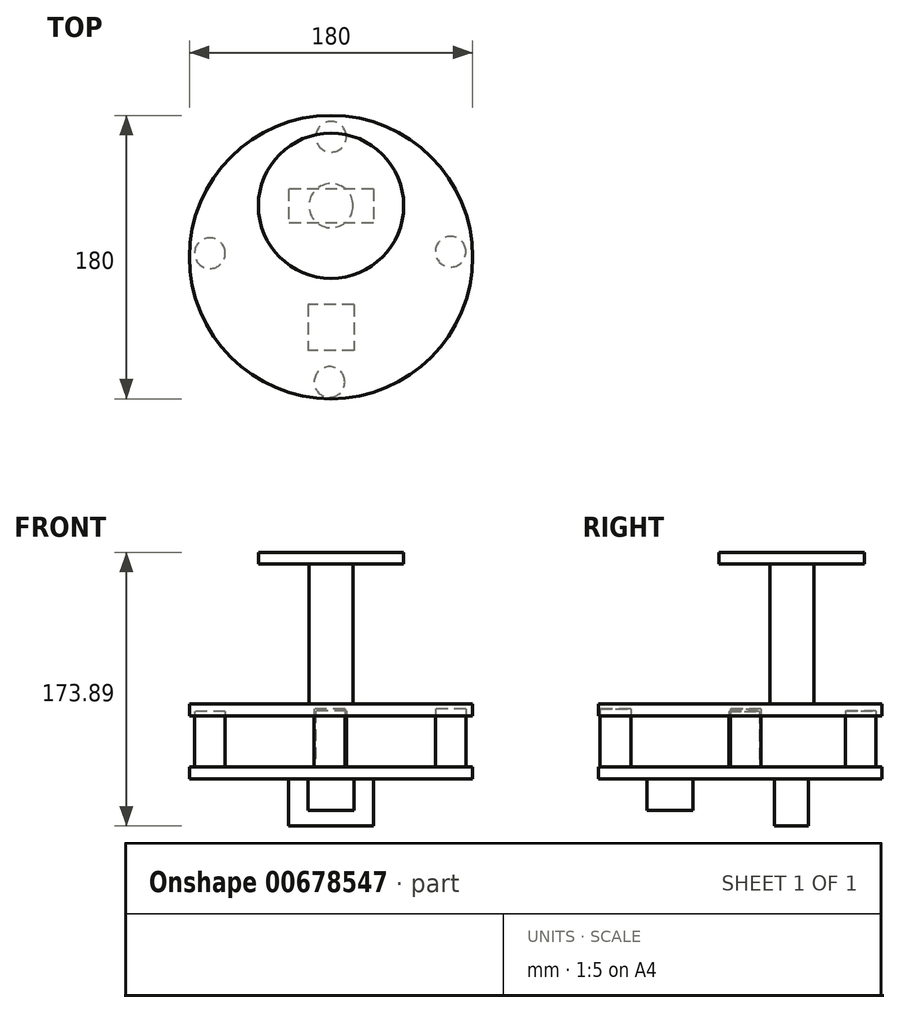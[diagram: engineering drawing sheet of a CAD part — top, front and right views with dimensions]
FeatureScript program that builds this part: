
annotation { "Feature Type Name" : "Feature", "Feature Type Description" : "" }
export const myFeature = defineFeature(function(context is Context, id is Id, definition is map)
    precondition{}
    {
        {
            var Q0;
            Q0=qCreatedBy(makeId("Top.planeOp"),FACE);
            var sketch = newSketch(context, id + "F0", { "sketchPlane" : qUnion([Q0])});
            skCircle(sketch, "E0", {"center": v(0, -4.4) * mm, "radius": 90 * mm});
            skSolve(sketch);
        }
        {
            var Q0;
            Q0 = qSketchRegion(id + "F0", true);
            extrude(context, id + "F1", {"entities" : qUnion([Q0]), "oppositeDirection" : true, "depth" : 7.5 * mm, "offsetDistance" : 25.4 * mm});
        }
        {
            var Q0;
            Q0=makeQuery(id+"F1.opExtrude","SWEPT_BODY",BODY,{"disambiguationData":[OSD([sQuery(id+"F0.wireOp",EDGE,"E0")])]});
            transform(context, id + "F2", {"entities" : qUnion([Q0]), "transformType" : TransformType.TRANSLATION_3D, "dx" : 0 * mm, "dy" : 0 * mm, "dz" : 40 * mm, "makeCopy" : true});
        }
        {
            var Q0;
            Q0=makeQuery(id+"F2.opPattern","COPY",BODY,{"derivedFrom":makeQuery(id+"F1.opExtrude","SWEPT_BODY",BODY,{"disambiguationData":[OSD([sQuery(id+"F0.wireOp",EDGE,"E0")])]}),"instanceName":"1"});
            transform(context, id + "F3", {"entities" : qUnion([Q0]), "transformType" : TransformType.TRANSLATION_3D, "dx" : 0 * mm, "dy" : 0 * mm, "dz" : 0 * mm, "makeCopy" : true});
        }
        {
            var Q0;
            Q0=makeQuery(id+"F2.opPattern","COPY",FACE,{"derivedFrom":makeQuery(id+"F1.opExtrude","CAP_FACE",FACE,{"disambiguationData":[OSD([sQuery(id+"F0.wireOp",EDGE,"E0")])],"isStart":true}),"instanceName":"1"});
            var sketch = newSketch(context, id + "F4", { "sketchPlane" : qUnion([Q0])});
            skLineSegment(sketch, "E1", {"start": v(0, 0) * mm, "end": v(0, 28.23) * mm});
            skCircle(sketch, "E2", {"center": v(0, 28.23) * mm, "radius": 14.02 * mm});
            skSolve(sketch);
        }
        {
            var Q0;
            Q0 = qSketchRegion(id + "F4", true);
            extrude(context, id + "F5", {"entities" : qUnion([Q0]), "depth" : 88.9 * mm, "offsetDistance" : 25.4 * mm});
        }
        {
            var Q0;
            Q0=makeQuery(id+"F5.opExtrude","CAP_FACE",FACE,{"disambiguationData":[OSD([sQuery(id+"F4.wireOp",EDGE,"E2")])],"isStart":false});
            var sketch = newSketch(context, id + "F6", { "sketchPlane" : qUnion([Q0])});
            skCircle(sketch, "E3", {"center": v(0, 28.23) * mm, "radius": 46.13 * mm});
            skSolve(sketch);
        }
        {
            var Q0;
            Q0 = qSketchRegion(id + "F6", true);
            extrude(context, id + "F7", {"entities" : qUnion([Q0]), "operationType" : NewBodyOperationType.ADD, "depth" : 7.5 * mm, "offsetDistance" : 25.4 * mm});
        }
        {
            var Q0;
            Q0=makeQuery(id+"F1.opExtrude","CAP_FACE",FACE,{"disambiguationData":[OSD([sQuery(id+"F0.wireOp",EDGE,"E0")])],"isStart":false});
            var sketch = newSketch(context, id + "F8", { "sketchPlane" : qUnion([Q0])});
            skLineSegment(sketch, "E4", {"start": v(0, 0) * mm, "end": v(0, -28) * mm});
            skLineSegment(sketch, "E5.bottom", {"start": v(26.89, -38.8) * mm, "end": v(-26.89, -38.8) * mm});
            skLineSegment(sketch, "E5.top", {"start": v(26.89, -17.21) * mm, "end": v(-26.89, -17.21) * mm});
            skLineSegment(sketch, "E5.left", {"start": v(26.89, -38.8) * mm, "end": v(26.89, -17.21) * mm});
            skLineSegment(sketch, "E5.right", {"start": v(-26.89, -38.8) * mm, "end": v(-26.89, -17.21) * mm});
            skPoint(sketch, "E5.middle", {"position": v(0, -28) * mm});
            skLineSegment(sketch, "E6", {"start": v(0, 0) * mm, "end": v(0, 49.18) * mm});
            skLineSegment(sketch, "E7.bottom", {"start": v(14.6, 34.57) * mm, "end": v(-14.6, 34.57) * mm});
            skLineSegment(sketch, "E7.top", {"start": v(14.6, 63.78) * mm, "end": v(-14.6, 63.78) * mm});
            skLineSegment(sketch, "E7.left", {"start": v(14.6, 34.57) * mm, "end": v(14.6, 63.78) * mm});
            skLineSegment(sketch, "E7.right", {"start": v(-14.6, 34.57) * mm, "end": v(-14.6, 63.78) * mm});
            skPoint(sketch, "E7.middle", {"position": v(0, 49.18) * mm});
            skSolve(sketch);
        }
        {
            var Q0;
            Q0=makeQuery(id+"F8.imprint","IMPRINT",FACE,{"disambiguationData":[TD([[makeQuery(id+"F8.imprint","IMPRINT",EDGE,{"derivedFrom":sQuery(id+"F8.wireOp",EDGE,"E5.bottom")}),-1.0]])]});
            extrude(context, id + "F9", {"entities" : qUnion([Q0]), "operationType" : NewBodyOperationType.ADD, "depth" : 30 * mm, "offsetDistance" : 25.4 * mm});
        }
        {
            var Q0;
            Q0=makeQuery(id+"F8.imprint","IMPRINT",FACE,{"disambiguationData":[TD([[makeQuery(id+"F8.imprint","IMPRINT",EDGE,{"derivedFrom":sQuery(id+"F8.wireOp",EDGE,"E7.top")}),1.0]])]});
            extrude(context, id + "F10", {"entities" : qUnion([Q0]), "operationType" : NewBodyOperationType.ADD, "depth" : 20 * mm, "offsetDistance" : 25.4 * mm});
        }
        {
            var Q0;
            Q0=qCreatedBy(makeId("Top.planeOp"),FACE);
            var sketch = newSketch(context, id + "F11", { "sketchPlane" : qUnion([Q0])});
            skCircle(sketch, "E8", {"center": v(0, 72.04) * mm, "radius": 9.73 * mm});
            skCircle(sketch, "E9", {"center": v(75.93, -0.98) * mm, "radius": 9.73 * mm});
            skCircle(sketch, "E10", {"center": v(-0.98, -83.74) * mm, "radius": 9.73 * mm});
            skCircle(sketch, "E11", {"center": v(-76.93, -1.95) * mm, "radius": 9.73 * mm});
            skSolve(sketch);
        }
        {
            var Q0;
            Q0=makeQuery(id+"F11.imprint","IMPRINT",FACE,{"disambiguationData":[TD([[makeQuery(id+"F11.imprint","IMPRINT",EDGE,{"derivedFrom":sQuery(id+"F11.wireOp",EDGE,"E10")}),1.0]])]});
            extrude(context, id + "F12", {"entities" : qUnion([Q0]), "depth" : 37.08 * mm, "offsetDistance" : 25.4 * mm});
        }
        {
            var Q0;
            Q0=makeQuery(id+"F11.imprint","IMPRINT",FACE,{"disambiguationData":[TD([[makeQuery(id+"F11.imprint","IMPRINT",EDGE,{"derivedFrom":sQuery(id+"F11.wireOp",EDGE,"E9")}),1.0]])]});
            extrude(context, id + "F13", {"entities" : qUnion([Q0]), "depth" : 37.08 * mm, "offsetDistance" : 25.4 * mm});
        }
        {
            var Q0;
            Q0=makeQuery(id+"F11.imprint","IMPRINT",FACE,{"disambiguationData":[TD([[makeQuery(id+"F11.imprint","IMPRINT",EDGE,{"derivedFrom":sQuery(id+"F11.wireOp",EDGE,"E11")}),1.0]])]});
            extrude(context, id + "F14", {"entities" : qUnion([Q0]), "depth" : 35.3 * mm, "offsetDistance" : 25.4 * mm});
        }
        {
            var Q0;
            Q0=makeQuery(id+"F11.imprint","IMPRINT",FACE,{"disambiguationData":[TD([[makeQuery(id+"F11.imprint","IMPRINT",EDGE,{"derivedFrom":sQuery(id+"F11.wireOp",EDGE,"E8")}),1.0]])]});
            extrude(context, id + "F15", {"entities" : qUnion([Q0]), "depth" : 35.56 * mm, "offsetDistance" : 25.4 * mm});
        }
    });
